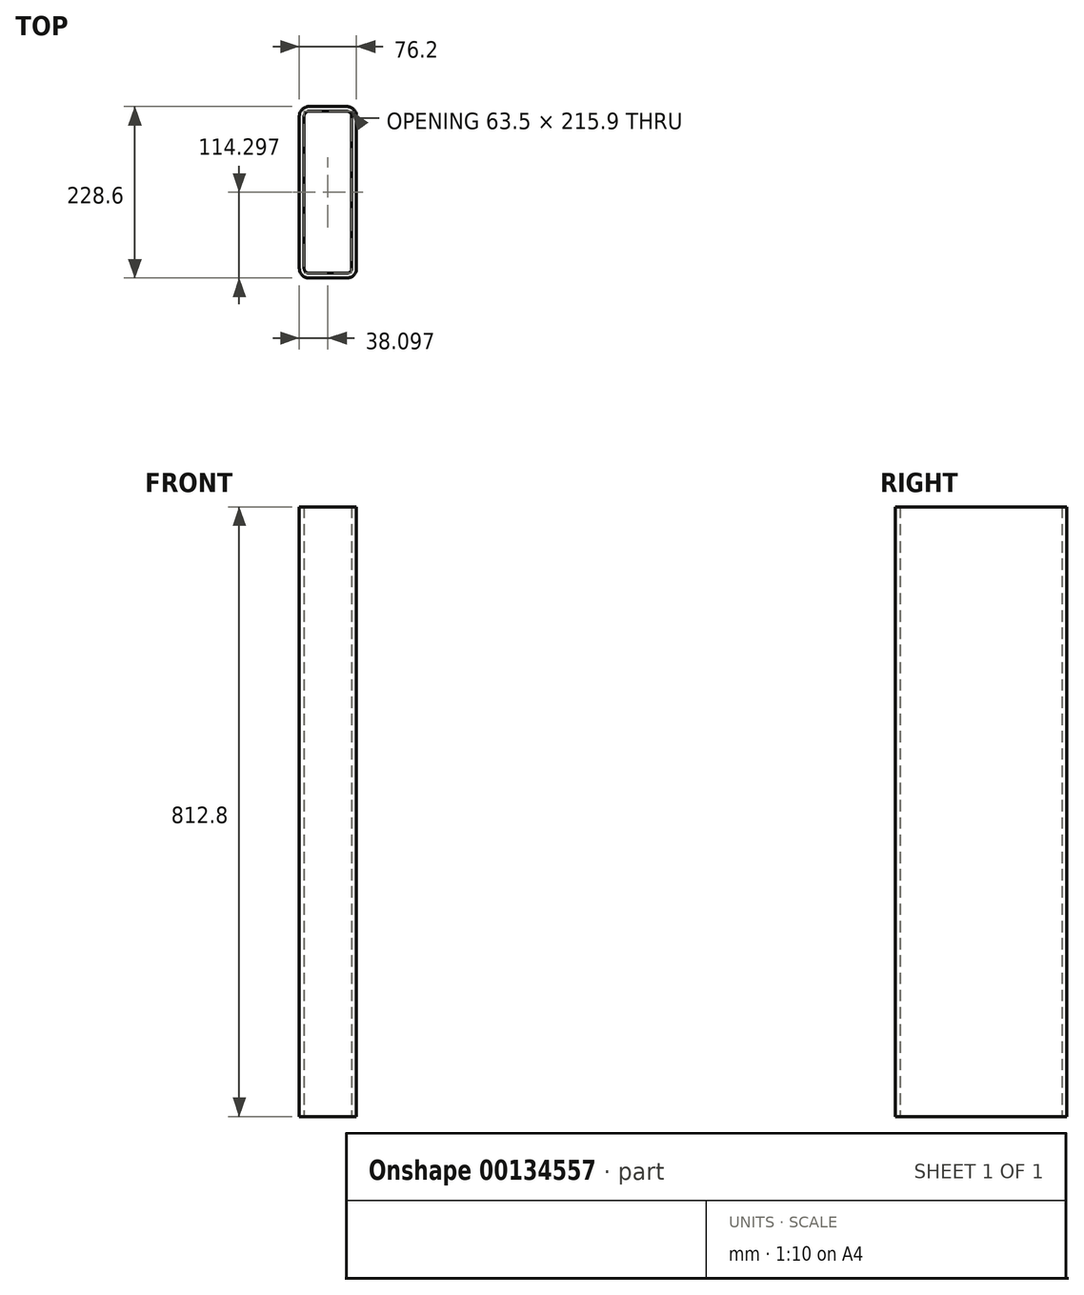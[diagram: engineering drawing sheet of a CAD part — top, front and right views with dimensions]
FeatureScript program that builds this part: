
annotation { "Feature Type Name" : "Feature", "Feature Type Description" : "" }
export const myFeature = defineFeature(function(context is Context, id is Id, definition is map)
    precondition{}
    {
        {
            var Q0;
            Q0=qCreatedBy(makeId("Top.planeOp"),FACE);
            var sketch = newSketch(context, id + "F0", { "sketchPlane" : qUnion([Q0])});
            skLineSegment(sketch, "E0", {"start": v(-23.51, 29.9) * mm, "end": v(27.29, 29.9) * mm});
            skLineSegment(sketch, "E1", {"start": v(39.99, 17.2) * mm, "end": v(39.99, -186) * mm});
            skLineSegment(sketch, "E2", {"start": v(27.29, -198.7) * mm, "end": v(-23.51, -198.7) * mm});
            skLineSegment(sketch, "E3", {"start": v(-36.21, -186) * mm, "end": v(-36.21, 17.2) * mm});
            skPoint(sketch, "E4.visualSharp", {"position": v(-36.21, 29.9) * mm});
            skArc(sketch, "E4.filletArc", {"start": v(-23.51, 29.9) * mm, "mid": v(-32.5, 26.18) * mm, "end": v(-36.21, 17.2) * mm});
            skPoint(sketch, "E5.visualSharp", {"position": v(39.99, 29.9) * mm});
            skArc(sketch, "E5.filletArc", {"start": v(39.99, 17.2) * mm, "mid": v(36.27, 26.18) * mm, "end": v(27.29, 29.9) * mm});
            skPoint(sketch, "E6.visualSharp", {"position": v(39.99, -198.7) * mm});
            skArc(sketch, "E6.filletArc", {"start": v(27.29, -198.7) * mm, "mid": v(36.27, -194.98) * mm, "end": v(39.99, -186) * mm});
            skPoint(sketch, "E7.visualSharp", {"position": v(-36.21, -198.7) * mm});
            skArc(sketch, "E7.filletArc", {"start": v(-36.21, -186) * mm, "mid": v(-32.5, -194.98) * mm, "end": v(-23.51, -198.7) * mm});
            skArc(sketch, "E8.0", {"start": v(-29.86, -186) * mm, "mid": v(-28, -190.5) * mm, "end": v(-23.51, -192.35) * mm});
            skLineSegment(sketch, "E8.1", {"start": v(27.29, -192.35) * mm, "end": v(-23.51, -192.35) * mm});
            skLineSegment(sketch, "E8.2", {"start": v(-29.86, -186) * mm, "end": v(-29.86, 17.2) * mm});
            skArc(sketch, "E8.3", {"start": v(27.29, -192.35) * mm, "mid": v(31.78, -190.5) * mm, "end": v(33.64, -186) * mm});
            skArc(sketch, "E8.4", {"start": v(-23.51, 23.55) * mm, "mid": v(-28, 21.69) * mm, "end": v(-29.86, 17.2) * mm});
            skLineSegment(sketch, "E8.5", {"start": v(-23.51, 23.55) * mm, "end": v(27.29, 23.55) * mm});
            skArc(sketch, "E8.6", {"start": v(33.64, 17.2) * mm, "mid": v(31.78, 21.69) * mm, "end": v(27.29, 23.55) * mm});
            skLineSegment(sketch, "E8.7", {"start": v(33.64, 17.2) * mm, "end": v(33.64, -186) * mm});
            skSolve(sketch);
        }
        {
            var Q0;
            Q0=makeQuery(id+"F0.imprint","IMPRINT",FACE,{"disambiguationData":[TD([[makeQuery(id+"F0.imprint","IMPRINT",EDGE,{"derivedFrom":sQuery(id+"F0.wireOp",EDGE,"E0")}),-1.0]])]});
            extrude(context, id + "F1", {"entities" : qUnion([Q0]), "depth" : 812.8 * mm});
        }
    });
